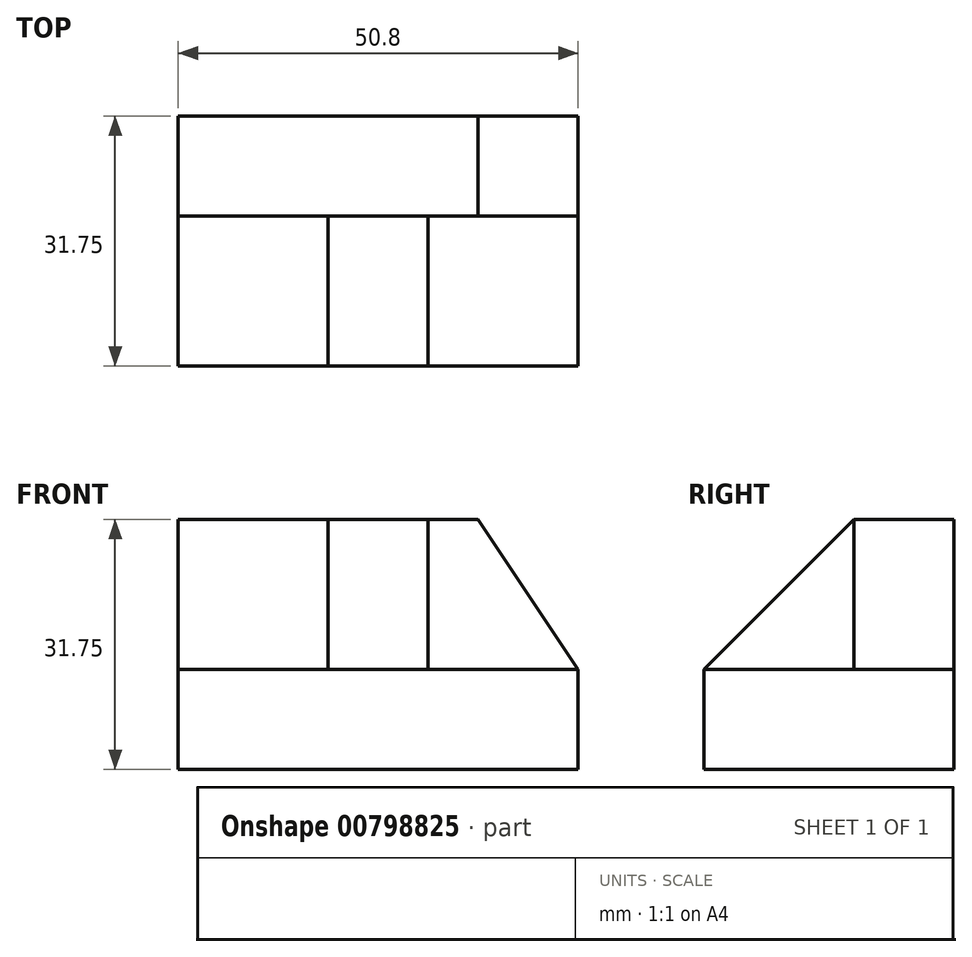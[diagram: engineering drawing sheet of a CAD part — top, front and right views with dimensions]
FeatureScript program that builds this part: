
annotation { "Feature Type Name" : "Feature", "Feature Type Description" : "" }
export const myFeature = defineFeature(function(context is Context, id is Id, definition is map)
    precondition{}
    {
        {
            var Q0;
            Q0=qCreatedBy(makeId("Front.planeOp"),FACE);
            var sketch = newSketch(context, id + "F0", { "sketchPlane" : qUnion([Q0])});
            skLineSegment(sketch, "E0", {"start": v(0, 0) * mm, "end": v(50.8, 0) * mm});
            skLineSegment(sketch, "E1", {"start": v(50.8, 0) * mm, "end": v(50.8, 12.7) * mm});
            skLineSegment(sketch, "E2", {"start": v(50.8, 12.7) * mm, "end": v(0, 12.7) * mm});
            skLineSegment(sketch, "E3", {"start": v(0, 12.7) * mm, "end": v(0, 0) * mm});
            skSolve(sketch);
        }
        {
            var Q0;
            Q0=makeQuery(id+"F0.imprint","IMPRINT",FACE,{"disambiguationData":[TD([[makeQuery(id+"F0.imprint","IMPRINT",EDGE,{"derivedFrom":sQuery(id+"F0.wireOp",EDGE,"E0")}),1.0]])]});
            extrude(context, id + "F1", {"entities" : qUnion([Q0]), "depth" : 31.75 * mm, "offsetDistance" : 25.4 * mm});
        }
        {
            var Q0;
            Q0=makeQuery(id+"F1.opExtrude","SWEPT_FACE",FACE,{"disambiguationData":[OSD([sQuery(id+"F0.wireOp",EDGE,"E2")])]});
            var sketch = newSketch(context, id + "F2", { "sketchPlane" : qUnion([Q0])});
            skLineSegment(sketch, "E4", {"start": v(50.8, 0) * mm, "end": v(50.8, -12.7) * mm});
            skLineSegment(sketch, "E5", {"start": v(50.8, -12.7) * mm, "end": v(0, -12.7) * mm});
            skSolve(sketch);
        }
        {
            var Q0;
            Q0=makeQuery(id+"F2.imprint","IMPRINT",FACE,{"disambiguationData":[TD([[makeQuery(id+"F2.imprint","IMPRINT",EDGE,{"derivedFrom":sQuery(id+"F2.wireOp",EDGE,"E4")}),1.0]])]});
            extrude(context, id + "F3", {"entities" : qUnion([Q0]), "operationType" : NewBodyOperationType.ADD, "depth" : 19.05 * mm, "offsetDistance" : 25.4 * mm});
        }
        {
            var Q0;
            Q0=makeQuery(id+"F3.opExtrude","SWEPT_FACE",FACE,{"disambiguationData":[OSD([sQuery(id+"F2.wireOp",EDGE,"E5")])]});
            var sketch = newSketch(context, id + "F4", { "sketchPlane" : qUnion([Q0])});
            skLineSegment(sketch, "E6", {"start": v(0, 31.75) * mm, "end": v(38.1, 31.75) * mm});
            skLineSegment(sketch, "E7", {"start": v(38.1, 31.75) * mm, "end": v(50.8, 12.7) * mm});
            skSolve(sketch);
        }
        {
            var Q0;
            {var subQ0=sQuery(id+"F4.wireOp",EDGE,"E7");Q0=makeQuery(id+"F4.imprint","IMPRINT",FACE,{"disambiguationData":[TD([[makeQuery(id+"F4.imprint","IMPRINT",EDGE,{"derivedFrom":subQ0}),1.0]])]});}
            extrude(context, id + "F5", {"entities" : qUnion([Q0]), "operationType" : NewBodyOperationType.REMOVE, "endBound" : BoundingType.THROUGH_ALL, "oppositeDirection" : true, "depth" : 25.4 * mm, "offsetDistance" : 25.4 * mm});
        }
        {
            var Q0;
            Q0=makeQuery(id+"F3.opExtrude","SWEPT_FACE",FACE,{"disambiguationData":[OSD([sQuery(id+"F2.wireOp",EDGE,"E5")])]});
            var sketch = newSketch(context, id + "F6", { "sketchPlane" : qUnion([Q0])});
            skLineSegment(sketch, "E8", {"start": v(0, 31.75) * mm, "end": v(19.05, 31.75) * mm});
            skLineSegment(sketch, "E9", {"start": v(38.1, 31.75) * mm, "end": v(31.75, 31.75) * mm});
            skLineSegment(sketch, "E10", {"start": v(19.05, 31.75) * mm, "end": v(19.05, 12.7) * mm});
            skLineSegment(sketch, "E11", {"start": v(31.75, 31.75) * mm, "end": v(31.75, 12.7) * mm});
            skSolve(sketch);
        }
        {
            var Q0;
            {var subQ0=sQuery(id+"F6.wireOp",EDGE,"E10");Q0=makeQuery(id+"F6.imprint","IMPRINT",FACE,{"disambiguationData":[TD([[makeQuery(id+"F6.imprint","IMPRINT",EDGE,{"derivedFrom":subQ0}),1.0]])]});}
            extrude(context, id + "F7", {"entities" : qUnion([Q0]), "operationType" : NewBodyOperationType.ADD, "depth" : 19.05 * mm, "offsetDistance" : 25.4 * mm});
        }
        {
            var Q0;
            Q0=makeQuery(id+"F7.opExtrude","SWEPT_FACE",FACE,{"disambiguationData":[OSD([sQuery(id+"F6.wireOp",EDGE,"E11")])]});
            var sketch = newSketch(context, id + "F8", { "sketchPlane" : qUnion([Q0])});
            skLineSegment(sketch, "E12", {"start": v(-31.75, 12.7) * mm, "end": v(-12.7, 31.75) * mm});
            skSolve(sketch);
        }
        {
            var Q0;
            Q0=makeQuery(id+"F8.imprint","IMPRINT",FACE,{"disambiguationData":[TD([[makeQuery(id+"F8.imprint","IMPRINT",EDGE,{"derivedFrom":sQuery(id+"F8.wireOp",EDGE,"E12")}),1.0]])]});
            extrude(context, id + "F9", {"entities" : qUnion([Q0]), "operationType" : NewBodyOperationType.REMOVE, "endBound" : BoundingType.THROUGH_ALL, "oppositeDirection" : true, "depth" : 25.4 * mm, "offsetDistance" : 25.4 * mm});
        }
    });
